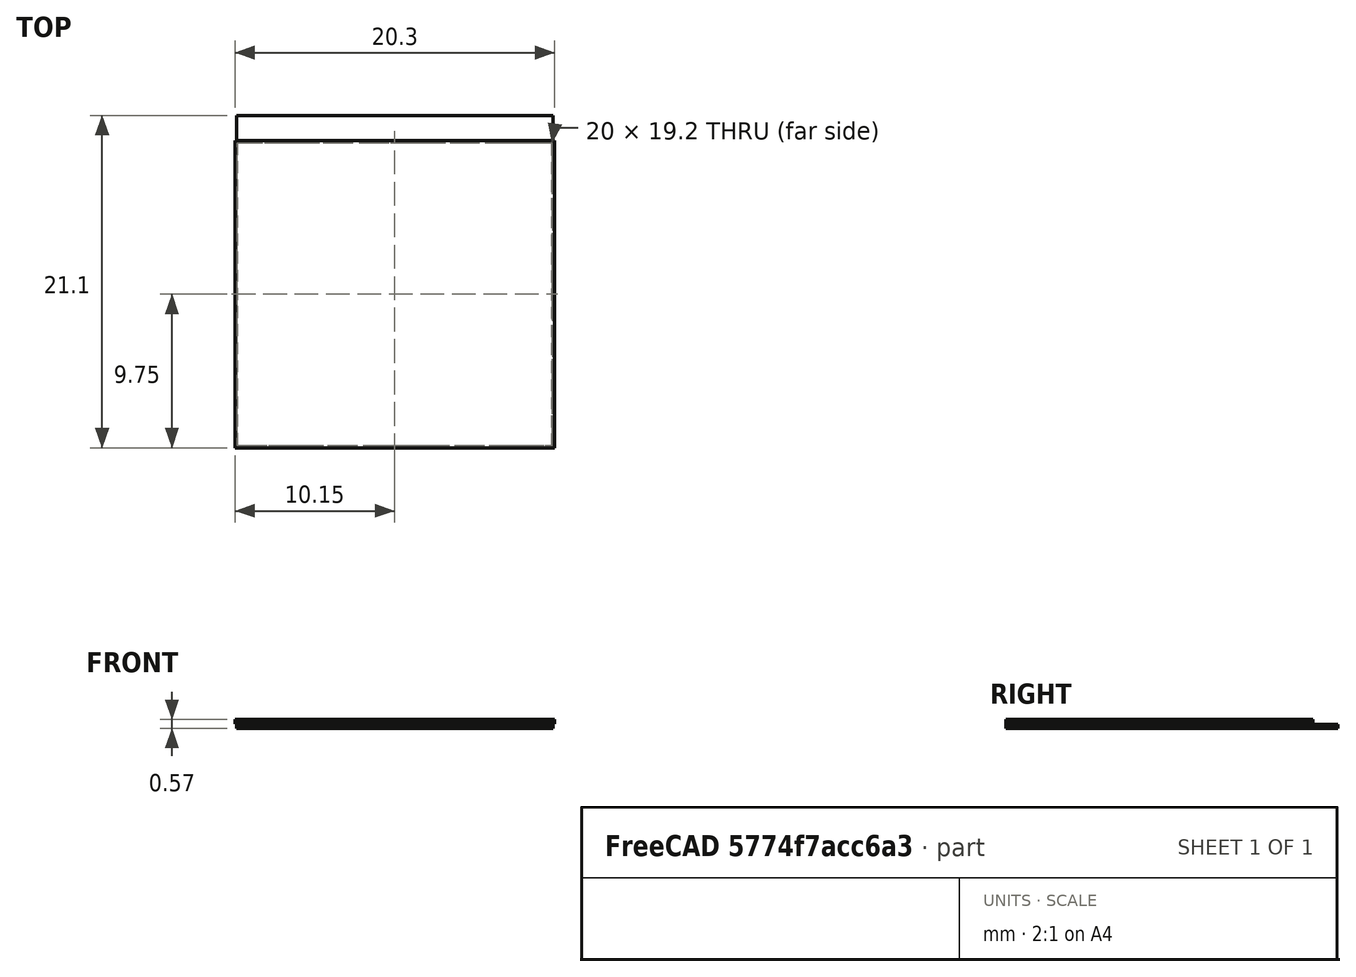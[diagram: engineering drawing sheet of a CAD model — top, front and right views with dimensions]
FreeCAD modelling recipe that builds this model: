
FCSTD DOCUMENT  (FreeCAD 0.17R13541 (Git))
Label: singlemodule
License: All rights reserved
LicenseURL: http://en.wikipedia.org/wiki/All_rights_reserved
objects: Sketcher::SketchObject×10, PartDesign::Pad×10, PartDesign::Body×10, PartDesign::ShapeBinder×9, App::MaterialObjectPython×7, Part::FeaturePython×2, Fem::FemSolverObjectPython×1, Fem::FemMeshObjectPython×1, Fem::ConstraintInitialTemperature×1, Fem::ConstraintHeatflux×1, Fem::ConstraintFixed×1, Fem::FemAnalysis×1
note: 51 computed .brp shape members not serialized (recipe doc carries the construction recipe); baked Part::Feature solids carry a one-line shape summary decoded from their .brp

FEATURE [Sketcher::SketchObject] Sketch
  MapMode = 5
  Support = -> [XY_Plane]
  sketch-geometry (4):
    g0: LineSegment StartX=0 StartY=0 StartZ=0 EndX=20.1 EndY=0 EndZ=0
    g1: LineSegment StartX=20.1 StartY=0 StartZ=0 EndX=20.1 EndY=21.1 EndZ=0
    g2: LineSegment StartX=20.1 StartY=21.1 StartZ=0 EndX=0 EndY=21.1 EndZ=0
    g3: LineSegment StartX=0 StartY=21.1 StartZ=0 EndX=0 EndY=0 EndZ=0
  constraints (11):
    c: Coincident(g0,g1)
    c: Coincident(g1,g2)
    c: Coincident(g2,g3)
    c: Coincident(g3,g0)
    c: Horizontal(g0)
    c: Horizontal(g2)
    c: Vertical(g1)
    c: Vertical(g3)
    c: Coincident(g0,g-1)
    c: DistanceX(g0,g0) = 20.1
    c: DistanceY(g3,g3) = 21.1
FEATURE [PartDesign::Pad] Pad
  Length = 0.15
  Length2 = 100
  Profile = -> Sketch
  Type = 0
FEATURE [PartDesign::Body] Body
  Group = -> [Sketch,Pad]
  Origin = -> Origin
  Tip = -> Pad
FEATURE [PartDesign::ShapeBinder] CopyPad
  Placement = pos=(0,0,0.15) rot=(0,0,1;0rad)
FEATURE [Sketcher::SketchObject] Sketch001
  MapMode = 5
  Placement = pos=(0,0,0.15) rot=(0,0,1;0rad)
  Support = -> [CopyPad]
  sketch-geometry (4):
    g0: LineSegment StartX=0.05 StartY=0.15 StartZ=0 EndX=20.05 EndY=0.15 EndZ=0
    g1: LineSegment StartX=20.05 StartY=0.15 StartZ=0 EndX=20.05 EndY=19.35 EndZ=0
    g2: LineSegment StartX=20.05 StartY=19.35 StartZ=0 EndX=0.05 EndY=19.35 EndZ=0
    g3: LineSegment StartX=0.05 StartY=19.35 StartZ=0 EndX=0.05 EndY=0.15 EndZ=0
  constraints (12):
    c: Coincident(g0,g1)
    c: Coincident(g1,g2)
    c: Coincident(g2,g3)
    c: Coincident(g3,g0)
    c: Horizontal(g0)
    c: Horizontal(g2)
    c: Vertical(g1)
    c: Vertical(g3)
    c: DistanceY(g-1,g0) = 0.15
    c: DistanceX(g-1,g0) = 0.05
    c: DistanceX(g0,g0) = 20
    c: DistanceY(g3,g3) = 19.2
FEATURE [PartDesign::Pad] Pad001
  Length = 0.025
  Length2 = 100
  Placement = pos=(0,0,0.15) rot=(0,0,1;0rad)
  Profile = -> Sketch001
  Type = 0
FEATURE [PartDesign::Body] Body001
  Group = -> [CopyPad,Sketch001,Pad001]
  Origin = -> Origin001
  Tip = -> Pad001
FEATURE [PartDesign::ShapeBinder] CopyPad001
  Placement = pos=(0,0,0.025) rot=(0,0,1;0rad)
FEATURE [Sketcher::SketchObject] Sketch002
  MapMode = 5
  Placement = pos=(0,0,0.175) rot=(0,0,1;0rad)
  Support = -> [CopyPad001]
  sketch-geometry (4):
    g0: LineSegment StartX=-0.1 StartY=0 StartZ=0 EndX=20.2 EndY=0 EndZ=0
    g1: LineSegment StartX=20.2 StartY=0 StartZ=0 EndX=20.2 EndY=19.5 EndZ=0
    g2: LineSegment StartX=20.2 StartY=19.5 StartZ=0 EndX=-0.1 EndY=19.5 EndZ=0
    g3: LineSegment StartX=-0.1 StartY=19.5 StartZ=0 EndX=-0.1 EndY=0 EndZ=0
  constraints (12):
    c: Coincident(g0,g1)
    c: Coincident(g1,g2)
    c: Coincident(g2,g3)
    c: Coincident(g3,g0)
    c: Horizontal(g0)
    c: Horizontal(g2)
    c: Vertical(g1)
    c: Vertical(g3)
    c: DistanceY(g0,g-1) = 0
    c: DistanceX(g0,g-1) = 0.1
    c: DistanceX(g0,g0) = 20.3
    c: DistanceY(g3,g3) = 19.5
FEATURE [PartDesign::Pad] Pad002
  Length = 0.15
  Length2 = 100
  Placement = pos=(0,0,0.025) rot=(0,0,1;0rad)
  Profile = -> Sketch002
  Type = 0
FEATURE [PartDesign::Body] Body002
  Group = -> [CopyPad001,Sketch002,Pad002]
  Origin = -> Origin002
  Tip = -> Pad002
FEATURE [PartDesign::ShapeBinder] CopyPad002
  Placement = pos=(0,0,0.15) rot=(0,0,1;0rad)
FEATURE [Sketcher::SketchObject] Sketch003
  MapMode = 5
  Placement = pos=(0,0,0.325) rot=(0,0,1;0rad)
  Support = -> [CopyPad002]
  sketch-geometry (4):
    g0: LineSegment StartX=-0.1 StartY=0 StartZ=0 EndX=20.2 EndY=0 EndZ=0
    g1: LineSegment StartX=20.2 StartY=0 StartZ=0 EndX=20.2 EndY=19.5 EndZ=0
    g2: LineSegment StartX=20.2 StartY=19.5 StartZ=0 EndX=-0.1 EndY=19.5 EndZ=0
    g3: LineSegment StartX=-0.1 StartY=19.5 StartZ=0 EndX=-0.1 EndY=0 EndZ=0
  constraints (12):
    c: Coincident(g0,g1)
    c: Coincident(g1,g2)
    c: Coincident(g2,g3)
    c: Coincident(g3,g0)
    c: Horizontal(g0)
    c: Horizontal(g2)
    c: Vertical(g1)
    c: Vertical(g3)
    c: DistanceY(g0,g-1) = 0
    c: DistanceX(g0,g-1) = 0.1
    c: DistanceX(g0,g0) = 20.3
    c: DistanceY(g3,g3) = 19.5
FEATURE [PartDesign::Pad] Pad003
  Length = 0.05
  Length2 = 100
  Placement = pos=(0,0,0.15) rot=(0,0,1;0rad)
  Profile = -> Sketch003
  Type = 0
FEATURE [PartDesign::Body] Body003
  Group = -> [CopyPad002,Sketch003,Pad003]
  Origin = -> Origin003
  Tip = -> Pad003
FEATURE [PartDesign::ShapeBinder] CopyPad003
  Placement = pos=(0,0,0.05) rot=(0,0,1;0rad)
FEATURE [Sketcher::SketchObject] Sketch004
  MapMode = 5
  Placement = pos=(0,0,0.375) rot=(0,0,1;0rad)
  Support = -> [CopyPad003]
  sketch-geometry (4):
    g0: LineSegment StartX=-0.1 StartY=0 StartZ=0 EndX=20.2 EndY=0 EndZ=0
    g1: LineSegment StartX=20.2 StartY=0 StartZ=0 EndX=20.2 EndY=19.5 EndZ=0
    g2: LineSegment StartX=20.2 StartY=19.5 StartZ=0 EndX=-0.1 EndY=19.5 EndZ=0
    g3: LineSegment StartX=-0.1 StartY=19.5 StartZ=0 EndX=-0.1 EndY=0 EndZ=0
  constraints (12):
    c: Coincident(g0,g1)
    c: Coincident(g1,g2)
    c: Coincident(g2,g3)
    c: Coincident(g3,g0)
    c: Horizontal(g0)
    c: Horizontal(g2)
    c: Vertical(g1)
    c: Vertical(g3)
    c: DistanceX(g0,g-1) = 0.1
    c: DistanceY(g0,g-1) = 0
    c: DistanceX(g0,g0) = 20.3
    c: DistanceY(g3,g3) = 19.5
FEATURE [PartDesign::Pad] Pad004
  Length = 0.0225
  Length2 = 100
  Placement = pos=(0,0,0.05) rot=(0,0,1;0rad)
  Profile = -> Sketch004
  Type = 0
FEATURE [PartDesign::Body] Body004
  Group = -> [CopyPad003,Sketch004,Pad004]
  Origin = -> Origin004
  Tip = -> Pad004
FEATURE [PartDesign::ShapeBinder] CopyPad004
  Placement = pos=(0,0,0.0225) rot=(0,0,1;0rad)
FEATURE [Sketcher::SketchObject] Sketch005
  MapMode = 5
  Placement = pos=(0,0,0.3975) rot=(0,0,1;0rad)
  Support = -> [CopyPad004]
  sketch-geometry (4):
    g0: LineSegment StartX=-0.1 StartY=0 StartZ=0 EndX=20.2 EndY=0 EndZ=0
    g1: LineSegment StartX=20.2 StartY=0 StartZ=0 EndX=20.2 EndY=19.5 EndZ=0
    g2: LineSegment StartX=20.2 StartY=19.5 StartZ=0 EndX=-0.1 EndY=19.5 EndZ=0
    g3: LineSegment StartX=-0.1 StartY=19.5 StartZ=0 EndX=-0.1 EndY=0 EndZ=0
  constraints (12):
    c: Coincident(g0,g1)
    c: Coincident(g1,g2)
    c: Coincident(g2,g3)
    c: Coincident(g3,g0)
    c: Horizontal(g0)
    c: Horizontal(g2)
    c: Vertical(g1)
    c: Vertical(g3)
    c: DistanceY(g0,g-1) = 0
    c: DistanceX(g0,g-1) = 0.1
    c: DistanceX(g0,g0) = 20.3
    c: DistanceY(g3,g3) = 19.5
FEATURE [PartDesign::Pad] Pad005
  Length = 0.0175
  Length2 = 100
  Placement = pos=(0,0,0.0225) rot=(0,0,1;0rad)
  Profile = -> Sketch005
  Type = 0
FEATURE [PartDesign::Body] Body005
  Group = -> [CopyPad004,Sketch005,Pad005]
  Origin = -> Origin005
  Tip = -> Pad005
FEATURE [PartDesign::ShapeBinder] CopyPad005
  Placement = pos=(0,0,0.0175) rot=(0,0,1;0rad)
FEATURE [Sketcher::SketchObject] Sketch006
  MapMode = 5
  Placement = pos=(0,0,0.415) rot=(0,0,1;0rad)
  Support = -> [CopyPad005]
  sketch-geometry (4):
    g0: LineSegment StartX=-0.1 StartY=0 StartZ=0 EndX=20.2 EndY=0 EndZ=0
    g1: LineSegment StartX=20.2 StartY=0 StartZ=0 EndX=20.2 EndY=19.5 EndZ=0
    g2: LineSegment StartX=20.2 StartY=19.5 StartZ=0 EndX=-0.1 EndY=19.5 EndZ=0
    g3: LineSegment StartX=-0.1 StartY=19.5 StartZ=0 EndX=-0.1 EndY=0 EndZ=0
  constraints (12):
    c: Coincident(g0,g1)
    c: Coincident(g1,g2)
    c: Coincident(g2,g3)
    c: Coincident(g3,g0)
    c: Horizontal(g0)
    c: Horizontal(g2)
    c: Vertical(g1)
    c: Vertical(g3)
    c: DistanceY(g0,g-1) = 0
    c: DistanceX(g0,g-1) = 0.1
    c: DistanceX(g0,g0) = 20.3
    c: DistanceY(g3,g3) = 19.5
FEATURE [PartDesign::Pad] Pad006
  Length = 0.02
  Length2 = 100
  Placement = pos=(0,0,0.0175) rot=(0,0,1;0rad)
  Profile = -> Sketch006
  Type = 0
FEATURE [PartDesign::Body] Body006
  Group = -> [CopyPad005,Sketch006,Pad006]
  Origin = -> Origin006
  Tip = -> Pad006
FEATURE [PartDesign::ShapeBinder] CopyPad006
  Placement = pos=(0,0,0.02) rot=(0,0,1;0rad)
FEATURE [Sketcher::SketchObject] Sketch007
  MapMode = 5
  Placement = pos=(0,0,0.435) rot=(0,0,1;0rad)
  Support = -> [CopyPad006]
  sketch-geometry (4):
    g0: LineSegment StartX=-0.1 StartY=0 StartZ=0 EndX=20.2 EndY=0 EndZ=0
    g1: LineSegment StartX=20.2 StartY=0 StartZ=0 EndX=20.2 EndY=19.5 EndZ=0
    g2: LineSegment StartX=20.2 StartY=19.5 StartZ=0 EndX=-0.1 EndY=19.5 EndZ=0
    g3: LineSegment StartX=-0.1 StartY=19.5 StartZ=0 EndX=-0.1 EndY=0 EndZ=0
  constraints (12):
    c: Coincident(g0,g1)
    c: Coincident(g1,g2)
    c: Coincident(g2,g3)
    c: Coincident(g3,g0)
    c: Horizontal(g0)
    c: Horizontal(g2)
    c: Vertical(g1)
    c: Vertical(g3)
    c: DistanceY(g0,g-1) = 0
    c: DistanceX(g0,g-1) = 0.1
    c: DistanceX(g0,g0) = 20.3
    c: DistanceY(g3,g3) = 19.5
FEATURE [PartDesign::Pad] Pad007
  Length = 0.0175
  Length2 = 100
  Placement = pos=(0,0,0.02) rot=(0,0,1;0rad)
  Profile = -> Sketch007
  Type = 0
FEATURE [PartDesign::Body] Body007
  Group = -> [CopyPad006,Sketch007,Pad007]
  Origin = -> Origin007
  Tip = -> Pad007
FEATURE [PartDesign::ShapeBinder] CopyPad007
  Placement = pos=(0,0,0.0175) rot=(0,0,1;0rad)
FEATURE [Sketcher::SketchObject] Sketch008
  MapMode = 5
  Placement = pos=(0,0,0.4525) rot=(0,0,1;0rad)
  Support = -> [CopyPad007]
  sketch-geometry (4):
    g0: LineSegment StartX=-0.1 StartY=0 StartZ=0 EndX=20.2 EndY=0 EndZ=0
    g1: LineSegment StartX=20.2 StartY=0 StartZ=0 EndX=20.2 EndY=19.5 EndZ=0
    g2: LineSegment StartX=20.2 StartY=19.5 StartZ=0 EndX=-0.1 EndY=19.5 EndZ=0
    g3: LineSegment StartX=-0.1 StartY=19.5 StartZ=0 EndX=-0.1 EndY=0 EndZ=0
  constraints (12):
    c: Coincident(g0,g1)
    c: Coincident(g1,g2)
    c: Coincident(g2,g3)
    c: Coincident(g3,g0)
    c: Horizontal(g0)
    c: Horizontal(g2)
    c: Vertical(g1)
    c: Vertical(g3)
    c: DistanceY(g0,g-1) = 0
    c: DistanceX(g0,g-1) = 0.1
    c: DistanceX(g0,g0) = 20.3
    c: DistanceY(g3,g3) = 19.5
FEATURE [PartDesign::Pad] Pad008
  Length = 0.0225
  Length2 = 100
  Placement = pos=(0,0,0.0175) rot=(0,0,1;0rad)
  Profile = -> Sketch008
  Type = 0
FEATURE [PartDesign::Body] Body008
  Group = -> [CopyPad007,Sketch008,Pad008]
  Origin = -> Origin008
  Tip = -> Pad008
FEATURE [PartDesign::ShapeBinder] CopyPad008
FEATURE [Sketcher::SketchObject] Sketch009
  MapMode = 5
  Placement = pos=(0,0,0) rot=(1,0,0;3.14159rad)
  Support = -> [CopyPad008]
  sketch-geometry (4):
    g0: LineSegment StartX=0 StartY=0 StartZ=0 EndX=20.1 EndY=0 EndZ=0
    g1: LineSegment StartX=20.1 StartY=0 StartZ=0 EndX=20.1 EndY=-21.1 EndZ=0
    g2: LineSegment StartX=20.1 StartY=-21.1 StartZ=0 EndX=0 EndY=-21.1 EndZ=0
    g3: LineSegment StartX=0 StartY=-21.1 StartZ=0 EndX=0 EndY=0 EndZ=0
  constraints (11):
    c: Coincident(g0,g1)
    c: Coincident(g1,g2)
    c: Coincident(g2,g3)
    c: Coincident(g3,g0)
    c: Horizontal(g0)
    c: Horizontal(g2)
    c: Vertical(g1)
    c: Vertical(g3)
    c: Coincident(g0,g-1)
    c: DistanceX(g2,g2) = 20.1
    c: DistanceY(g3,g3) = 21.1
FEATURE [PartDesign::Pad] Pad009
  Length = 0.1
  Length2 = 100
  Profile = -> Sketch009
  Type = 0
FEATURE [PartDesign::Body] Body009
  Group = -> [CopyPad008,Sketch009,Pad009]
  Origin = -> Origin009
  Tip = -> Pad009
FEATURE [Fem::FemSolverObjectPython] CalculiXccxTools  # FEM object (typed FeaturePython)
  AnalysisType = 2
  BeamShellResultOutput3D = false
  EigenmodeHighLimit = 1000000
  EigenmodeLowLimit = 0
  EigenmodesCount = 10
  GeometricalNonlinearity = 0
  IterationsControlParameterCutb = 0.25,0.5,0.75,0.85,,,1.5,
  IterationsControlParameterIter = 4,8,9,200,10,400,,200,,
  IterationsControlParameterTimeUse = false
  IterationsThermoMechMaximum = 2000
  IterationsUserDefinedIncrementations = false
  IterationsUserDefinedTimeStepLength = false
  MaterialNonlinearity = 0
  MatrixSolverType = 0
  SplitInputWriter = false
  ThermoMechSteadyState = true
  TimeEnd = 1
  TimeInitialStep = 1
FEATURE [Part::FeaturePython] BooleanFragments  # WARN: FeaturePython — macro-defined, semantics opaque (R4)
  Mode = 2
  Objects = -> [Body009,Body008,Body006,Body007,Body005,Body004,Body003,Body002,Body001,Body]
  Tolerance = 0
FEATURE [Part::FeaturePython] CompoundFilter  # WARN: FeaturePython — macro-defined, semantics opaque (R4)
  Base = -> BooleanFragments
  FilterType = 3
  Invert = false
  OverrideMaxVal = 0
  WindowFrom = 80
  WindowTo = 100
FEATURE [Fem::FemMeshObjectPython] FEMMeshGmsh  # FEM object (typed FeaturePython)
  Algorithm2D = 0
  Algorithm3D = 0
  CharacteristicLengthMax = 2
  CharacteristicLengthMin = 0
  CoherenceMesh = true
  ElementDimension = 0
  ElementOrder = 1
  GeometryTolerance = 1e-06
  GroupsOfNodes = false
  HighOrderOptimize = false
  OptimizeNetgen = false
  OptimizeStd = true
  Part = -> CompoundFilter
  RecombineAll = false
FEATURE [Fem::ConstraintInitialTemperature] FemConstraintInitialTemperature
  NormalDirection = (0,0,1)
  initialTemperature = 300
FEATURE [Fem::ConstraintHeatflux] FemConstraintHeatflux
  AmbientTemp = 213
  ConstraintType = 1
  DFlux = 0
  FilmCoef = 10
  NormalDirection = (0,-1,0)
  Normals = (394) [(0,-1,0),(0,-1,0),(0,-1,0),(0,-1,0),(0,-1,0),(0,-1,0),(0,-1,0),(0,-1,0),(0,-1,0),(0,-1,0),(0,-1,0),(0,-1,0),(0,-1,0),(0,-1,0),(0,-1,0),(0,-1,0),+378 more]
  Points = (394) [(0,0,-0.1),(10.05,0,-0.1),(20.1,0,-0.1),(0,0,-0.05),(10.05,0,-0.05),(20.1,0,-0.05),(0,0,0),(10.05,0,0),(20.1,0,0),(0,0,0.15),(10.05,0,0.15),+383 more]
  References = -> [CompoundFilter]
FEATURE [Fem::ConstraintFixed] FemConstraintFixed
  NormalDirection = (0,0,-1)
  Normals = (9) [(0,0,-1),(0,0,-1),(0,0,-1),(0,0,-1),(0,0,-1),(0,0,-1),(0,0,-1),(0,0,-1),(0,0,-1)]
  Points = (9) [(0,0,-0.1),(10.05,0,-0.1),(20.1,0,-0.1),(0,10.55,-0.1),(10.05,10.55,-0.1),(20.1,10.55,-0.1),(0,21.1,-0.1),(10.05,21.1,-0.1),(20.1,21.1,-0.1)]
  References = -> [CompoundFilter]
FEATURE [App::MaterialObjectPython] SolidMaterial  # material (typed FeaturePython)
  Category = 0
  Material = Density=2329.0 kg/m^3,Description=This is a not defined material,Father=None,Name=None,PoissonRatio=0.28,SpecificHeat=0.71 J/kg/K,SpecificPrice=0,+4 more (map truncated)
  References = -> [CompoundFilter]
FEATURE [App::MaterialObjectPython] SolidMaterial001  # material (typed FeaturePython)
  Category = 0
  Material = Density=2.356e+12 kg/m^3,Description=This is a not defined material,Father=None,Name=None,PoissonRatio=0.35,SpecificHeat=0.8 J/kg/K,SpecificPrice=0,+4 more (map truncated)
  References = -> [CompoundFilter]
FEATURE [App::MaterialObjectPython] SolidMaterial002  # material (typed FeaturePython)
  Category = 0
  Material = Density=1500.0 kg/m^3,Description=This is a not defined material,Father=None,Name=None,PoissonRatio=0.34,SpecificHeat=0.21 J/kg/K,SpecificPrice=0,+4 more (map truncated)
  References = -> [CompoundFilter]
FEATURE [App::MaterialObjectPython] SolidMaterial003  # material (typed FeaturePython)
  Category = 0
  Material = Density=142.0 kg/m^3,Description=This is a not defined material,Father=None,Name=None,PoissonRatio=0.34,SpecificHeat=1.09 J/kg/K,SpecificPrice=0,+4 more (map truncated)
  References = -> [CompoundFilter]
FEATURE [App::MaterialObjectPython] SolidMaterial004  # material (typed FeaturePython)
  Category = 0
  Material = Density=2809.7 kg/m^3,Description=This is a not defined material,Father=None,Name=None,PoissonRatio=0.341,SpecificHeat=0.8433 J/kg/K,SpecificPrice=0,+4 more (map truncated)
  References = -> [CompoundFilter]
FEATURE [App::MaterialObjectPython] SolidMaterial005  # material (typed FeaturePython)
  Category = 0
  Material = Density=7764.0 kg/m^3,Description=This is a not defined material,Father=None,Name=None,PoissonRatio=0.343,SpecificHeat=0.385 J/kg/K,SpecificPrice=0,+4 more (map truncated)
  References = -> [CompoundFilter]
FEATURE [App::MaterialObjectPython] SolidMaterial006  # material (typed FeaturePython)
  Category = 0
  Material = Density=1000.0 kg/m^3,Description=This is a not defined material,Father=None,Name=None,PoissonRatio=0.35,SpecificHeat=0.8 J/kg/K,SpecificPrice=0,+4 more (map truncated)
  References = -> [CompoundFilter]
FEATURE [Fem::FemAnalysis] Analysis
  Group = -> [CalculiXccxTools,FEMMeshGmsh,FemConstraintInitialTemperature,FemConstraintHeatflux,FemConstraintFixed,SolidMaterial,SolidMaterial001,SolidMaterial002,SolidMaterial003,SolidMaterial004,SolidMaterial005,SolidMaterial006]
